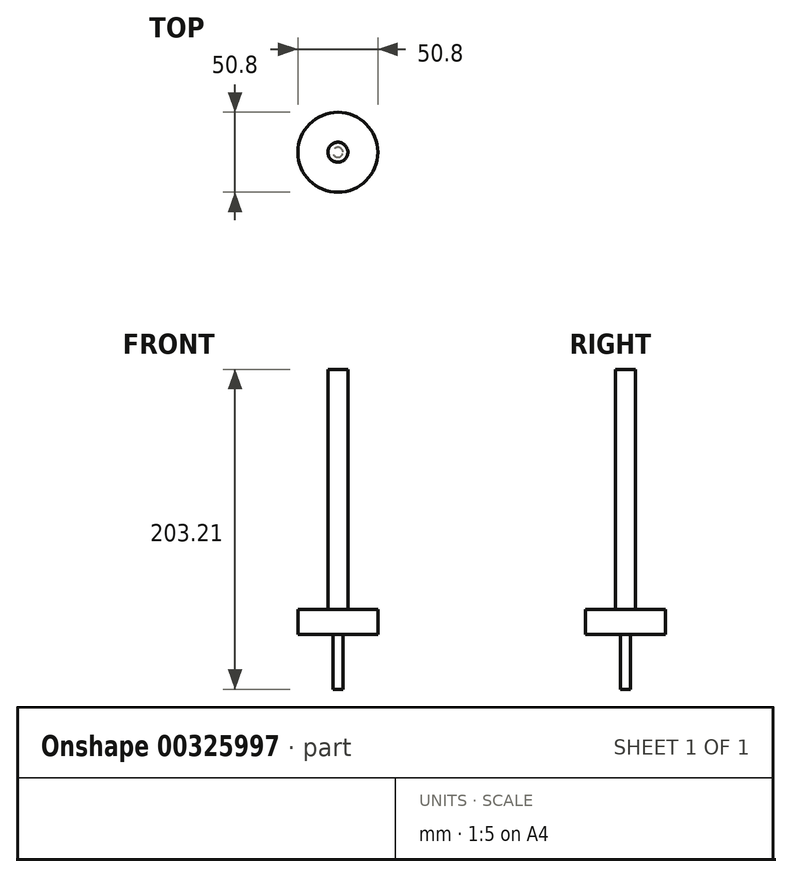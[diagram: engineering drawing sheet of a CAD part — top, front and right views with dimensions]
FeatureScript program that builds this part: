
annotation { "Feature Type Name" : "Feature", "Feature Type Description" : "" }
export const myFeature = defineFeature(function(context is Context, id is Id, definition is map)
    precondition{}
    {
        {
            var Q0;
            Q0=qCreatedBy(makeId("Front.planeOp"),FACE);
            var sketch = newSketch(context, id + "F0", { "sketchPlane" : qUnion([Q0])});
            skLineSegment(sketch, "E0", {"start": v(0, -34.93) * mm, "end": v(0, 168.28) * mm});
            skLineSegment(sketch, "E1", {"start": v(-6.35, 168.28) * mm, "end": v(-6.35, 15.88) * mm});
            skLineSegment(sketch, "E2", {"start": v(-25.4, 15.88) * mm, "end": v(-25.4, 0) * mm});
            skLineSegment(sketch, "E3", {"start": v(-3.17, -34.93) * mm, "end": v(0, -34.93) * mm});
            skLineSegment(sketch, "E4", {"start": v(-25.4, 0) * mm, "end": v(-3.17, 0) * mm});
            skLineSegment(sketch, "E5", {"start": v(-25.4, 15.88) * mm, "end": v(-6.35, 15.88) * mm});
            skLineSegment(sketch, "E6", {"start": v(-6.35, 168.28) * mm, "end": v(0, 168.28) * mm});
            skLineSegment(sketch, "E7", {"start": v(-3.17, 0) * mm, "end": v(-3.17, -34.93) * mm});
            skSolve(sketch);
        }
        {
            var Q0;
            Q0=makeQuery(id+"F0.imprint","IMPRINT",FACE,{"disambiguationData":[TD([[makeQuery(id+"F0.imprint","IMPRINT",EDGE,{"derivedFrom":sQuery(id+"F0.wireOp",EDGE,"E0")}),1.0]])]});
            var Q1;
            Q1=sQuery(id+"F0.wireOp",EDGE,"E0");
            revolve(context, id + "F1", {"entities" : qUnion([Q0]), "axis" : qUnion([Q1]), "revolveType" : RevolveType.FULL});
        }
    });
